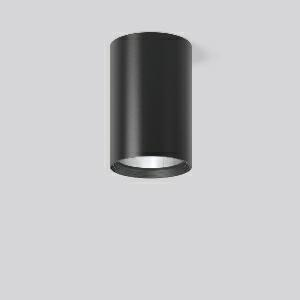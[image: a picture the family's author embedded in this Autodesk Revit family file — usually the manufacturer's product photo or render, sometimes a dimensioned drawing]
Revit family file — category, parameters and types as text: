
# Revit family: heledon_maxi_a_931224_003_76_41f9
name_source: partatom
category: Lighting Fixtures
units: mm (PartAtom-declared; Revit-internal decimal feet)

## family parameters
Cut with Voids When Loaded = No
Host = Face
Light Source = No
Part Type = Normal
Room Calculation Point = No
Round Connector Dimension = Use Diameter
Shared = No

## types (1)
- HELEDON maxi A (1 x LED Modul 930, 4300 lm, 3000)
    Apparent Load = 35 VA
    Approval mark = CE
    CIE Flux Codes = 100 100 100 100 100
    Color Rendering = 90
    Color Temperature = 3000
    Default Elevation = 1800 mm
    Description = Series: HELEDON maxi
Cylindrical surface-mounted downlight. Housing: die-cast aluminium, powder-coated. Internal ceiling frame polycarbonate with bayonet mounting. Black plastic ring and recessed LED to prevent glare from the side. Optical assembly with reflector made of MIRO-Silver with 98% total light reflection for outstanding efficiency - can be changed without tools. Best colour rendering index Ra>90. Suitable for Ceiling mounting. Easy installation with a separate ceiling frame with bayonet mounting and plug connection. Driver integrated. Connected via plug-in connector. High quality converter without flickering and stroboscopic effect. The following accessories can be mounted without use of tools: interchangeable lenses, decorative glasses, honeycomb louvre, clear and frosted diffusers, white interchangeable plastic ring. 
Colour: deep black, matt (RAL 9005)
Diameter: 123 mm
Height: 183 mm
Lamp: LED
Socket: without socket
Colour temperature: 3000K
Colour rendering index (CRI): 92
System power: 35 W
Rated luminous flux: 4300 lm
Luminous efficiency: 123 lm/W
Control gear: Converter, dimmable, DALI
Protection class: I
Type of protection: IP 20
    Height = 183 mm
    Lamp = 1 x LED Modul 930
    Lamp Light Flux = 4300 lm
    Lamp count = 1
    Length = 123 mm
    Lifetime = 50000 h
    Luminous efficacy = 123 lm/W
    Manufacturer = RZB
    ModVariant = No
    Model = 931224.003.76
    Mounting Place = Ceiling
    Mounting Type = Surface mounted
    Number of Poles = 1
    OnlyDefault = Yes
    Power Factor = 1
    Product Name = HELEDON maxi A
    Product group = Surface mounted downlights
    ProductGroupID = 302
    Protection Class = Protection class I
    Protection Degree = IP 20
    RLX_Detail_Level = 1
    RLX_Emergency_Light_Flux = 0 lm
    RLX_Emergency_Type = 0
    RLX_Emergency_Type_DB = No
    RlxData = <blob elided: 96737 chars, md5=bbff4c2b>
    Socket = socket
    Standby Power = 0 W
    System Light Flux = 4300 lm
    System Power = 35 W
    Type Comments = Product without accessories
    Type Image = 931192.003.jpg
    URL = http://relux.com
    VarID = ---
    Voltage = 230 V
    Voltage Range = 220-240 V
    Weight = 0.00 kg
    Width = 0 mm  [stored 0 ft]

note: [stored X ft] marks values corroborated as IEEE doubles in the binary element streams (Revit-internal decimal feet)

## geometry (parser evidence)
native form markers: Blend x4, Sweep x10
no freeform markers — native parametric forms only
